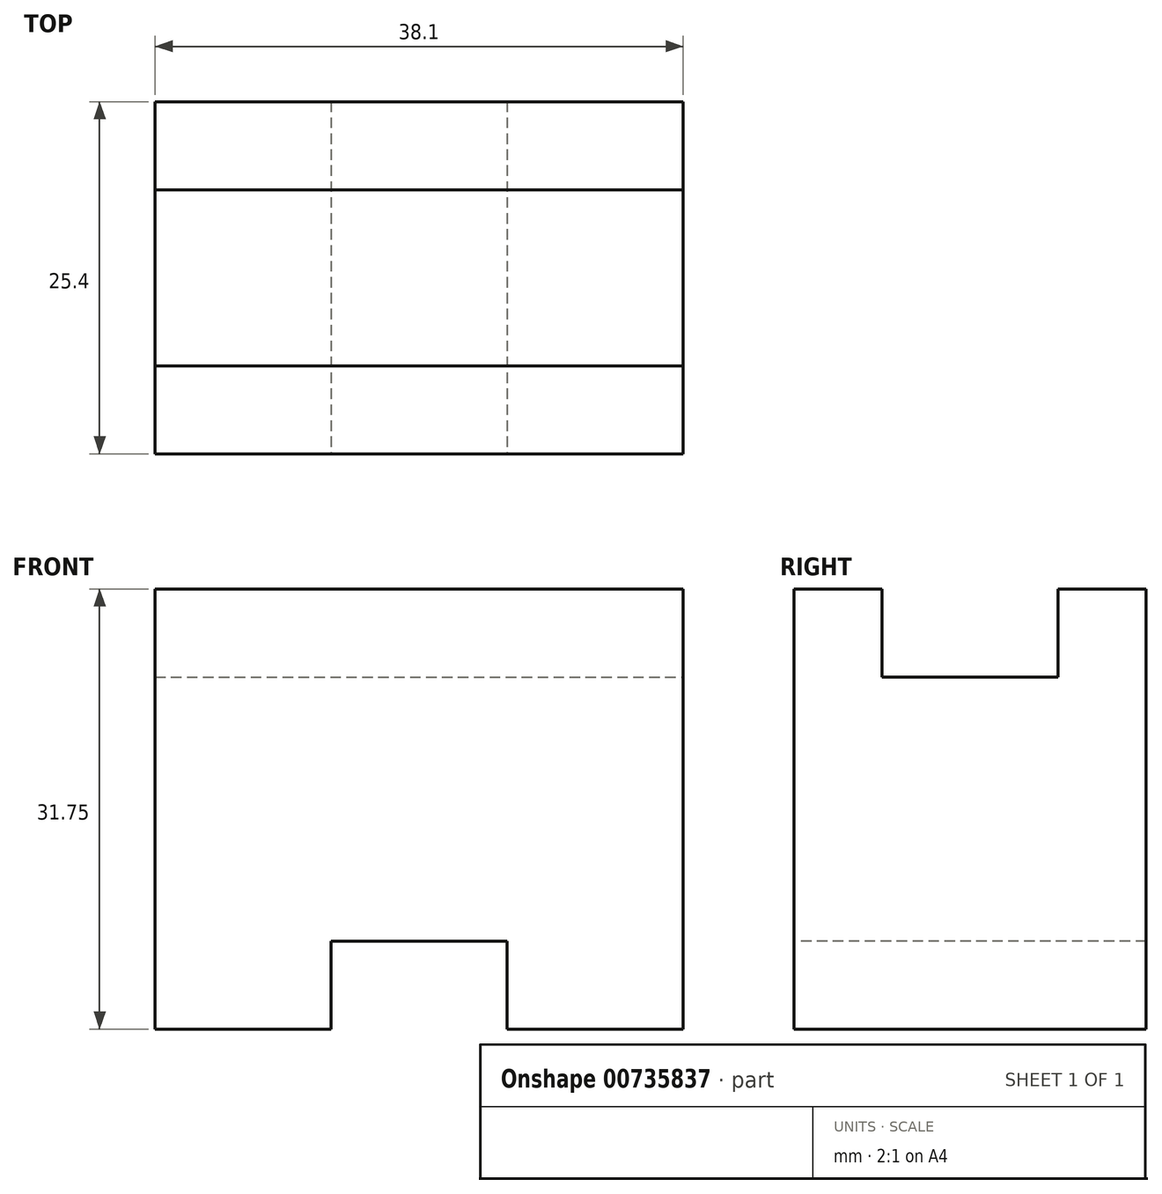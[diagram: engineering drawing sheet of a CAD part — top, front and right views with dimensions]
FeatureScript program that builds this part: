
annotation { "Feature Type Name" : "Feature", "Feature Type Description" : "" }
export const myFeature = defineFeature(function(context is Context, id is Id, definition is map)
    precondition{}
    {
        {
            var Q0;
            Q0=qCreatedBy(makeId("Front.planeOp"),FACE);
            var sketch = newSketch(context, id + "F0", { "sketchPlane" : qUnion([Q0])});
            skLineSegment(sketch, "E0", {"start": v(0, 0) * mm, "end": v(38.1, 0) * mm});
            skLineSegment(sketch, "E1", {"start": v(38.1, 0) * mm, "end": v(38.1, 31.75) * mm});
            skLineSegment(sketch, "E2", {"start": v(38.1, 31.75) * mm, "end": v(0, 31.75) * mm});
            skLineSegment(sketch, "E3", {"start": v(0, 31.75) * mm, "end": v(0, 0) * mm});
            skSolve(sketch);
        }
        {
            var Q0;
            Q0 = qSketchRegion(id + "F0", true);
            extrude(context, id + "F1", {"entities" : qUnion([Q0]), "depth" : 25.4 * mm, "offsetDistance" : 25.4 * mm});
        }
        {
            var Q0;
            Q0=makeQuery(id+"F1.opExtrude","CAP_FACE",FACE,{"disambiguationData":[OSD([sQuery(id+"F0.wireOp",EDGE,"E0"),sQuery(id+"F0.wireOp",EDGE,"E1"),sQuery(id+"F0.wireOp",EDGE,"E2"),sQuery(id+"F0.wireOp",EDGE,"E3")])],"isStart":false});
            var sketch = newSketch(context, id + "F2", { "sketchPlane" : qUnion([Q0])});
            skLineSegment(sketch, "E4", {"start": v(12.7, 0) * mm, "end": v(12.7, 6.35) * mm});
            skLineSegment(sketch, "E5", {"start": v(12.7, 6.35) * mm, "end": v(25.4, 6.35) * mm});
            skLineSegment(sketch, "E6", {"start": v(25.4, 6.35) * mm, "end": v(25.4, 0) * mm});
            skSolve(sketch);
        }
        {
            var Q0;
            Q0 = qSketchRegion(id + "F2", true);
            var Q1;
            {var subQ0=sQuery(id+"F2.wireOp",EDGE,"E4");Q1=makeQuery(id+"F2.imprint","IMPRINT",FACE,{"disambiguationData":[TD([[makeQuery(id+"F2.imprint","IMPRINT",EDGE,{"derivedFrom":subQ0}),-1.0]])]});}
            extrude(context, id + "F3", {"entities" : qUnion([Q0, Q1]), "operationType" : NewBodyOperationType.REMOVE, "oppositeDirection" : true, "depth" : 25.4 * mm, "offsetDistance" : 25.4 * mm});
        }
        {
            var Q0;
            Q0=makeQuery(id+"F1.opExtrude","SWEPT_FACE",FACE,{"disambiguationData":[OSD([sQuery(id+"F0.wireOp",EDGE,"E2")])]});
            var sketch = newSketch(context, id + "F4", { "sketchPlane" : qUnion([Q0])});
            skLineSegment(sketch, "E7", {"start": v(0, -6.35) * mm, "end": v(38.1, -6.35) * mm});
            skLineSegment(sketch, "E8", {"start": v(38.1, -6.35) * mm, "end": v(38.1, -19.05) * mm});
            skLineSegment(sketch, "E9", {"start": v(38.1, -19.05) * mm, "end": v(0, -19.05) * mm});
            skLineSegment(sketch, "E10", {"start": v(0, -19.05) * mm, "end": v(0, -6.35) * mm});
            skSolve(sketch);
        }
        {
            var Q0;
            Q0=makeQuery(id+"F4.imprint","IMPRINT",FACE,{"disambiguationData":[TD([[makeQuery(id+"F4.imprint","IMPRINT",EDGE,{"derivedFrom":sQuery(id+"F4.wireOp",EDGE,"E7")}),-1.0]])]});
            extrude(context, id + "F5", {"entities" : qUnion([Q0]), "operationType" : NewBodyOperationType.REMOVE, "oppositeDirection" : true, "depth" : 6.35 * mm, "offsetDistance" : 25.4 * mm});
        }
    });
